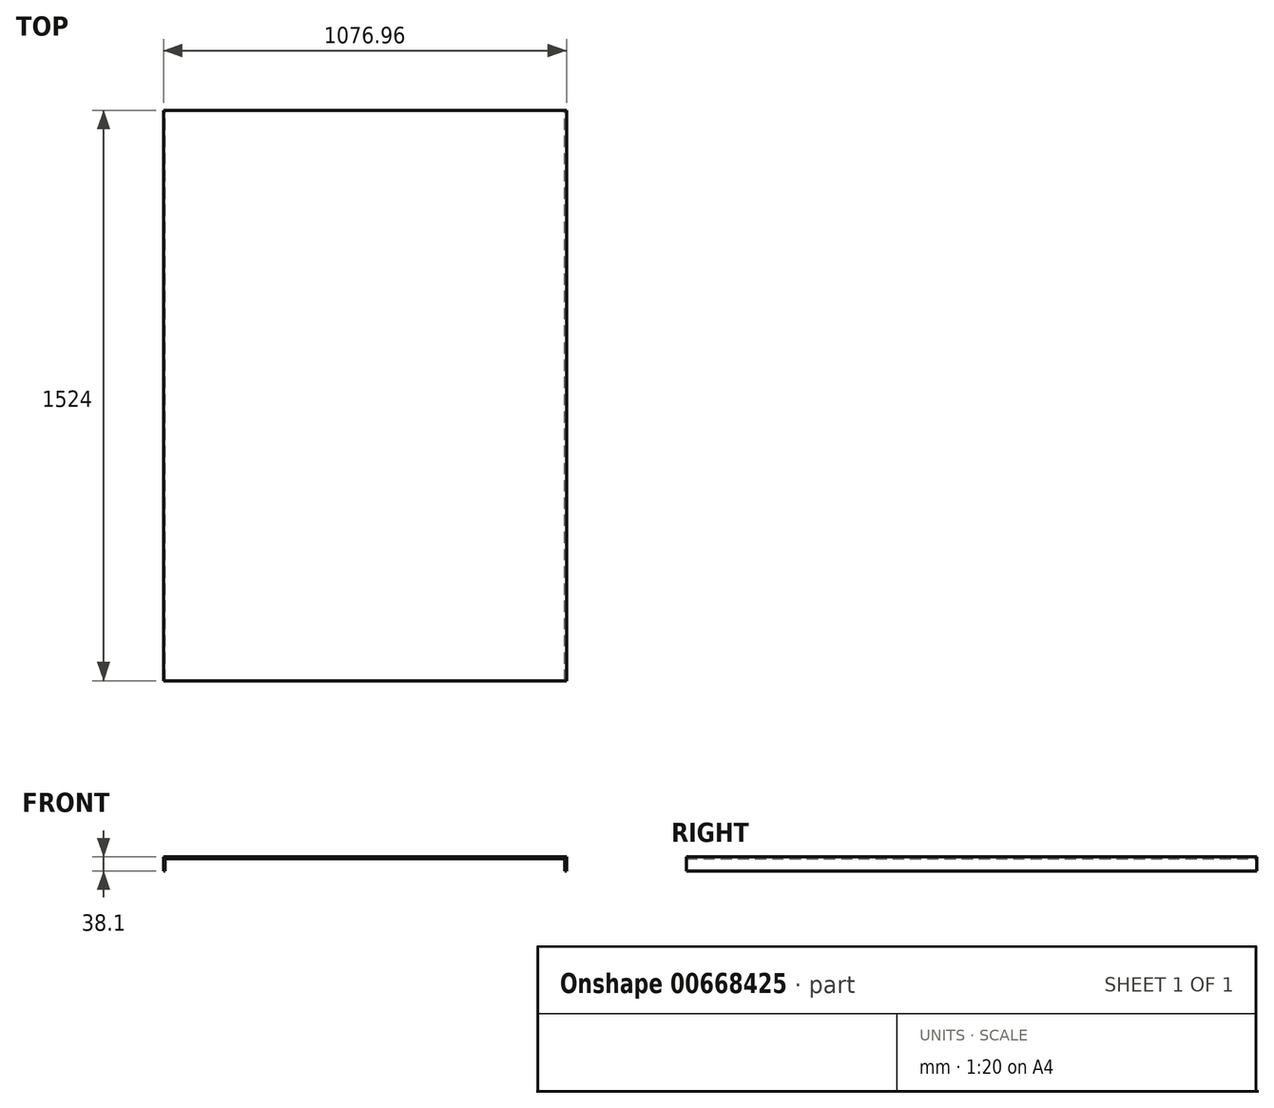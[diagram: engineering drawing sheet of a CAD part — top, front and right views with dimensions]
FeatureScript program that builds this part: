
annotation { "Feature Type Name" : "Feature", "Feature Type Description" : "" }
export const myFeature = defineFeature(function(context is Context, id is Id, definition is map)
    precondition{}
    {
        {
            var Q0;
            Q0=qCreatedBy(makeId("Front.planeOp"),FACE);
            var sketch = newSketch(context, id + "F0", { "sketchPlane" : qUnion([Q0])});
            skLineSegment(sketch, "E0.bottom", {"start": v(-104.04, -41.65) * mm, "end": v(972.92, -41.65) * mm});
            skLineSegment(sketch, "E0.top", {"start": v(-104.04, -36.87) * mm, "end": v(972.92, -36.87) * mm});
            skLineSegment(sketch, "E0.left", {"start": v(-104.04, -41.65) * mm, "end": v(-104.04, -36.87) * mm});
            skLineSegment(sketch, "E0.right", {"start": v(972.92, -41.65) * mm, "end": v(972.92, -36.87) * mm});
            skLineSegment(sketch, "E1.bottom", {"start": v(-104.04, -36.87) * mm, "end": v(-99.27, -36.87) * mm});
            skLineSegment(sketch, "E1.top", {"start": v(-104.04, -74.97) * mm, "end": v(-99.27, -74.97) * mm});
            skLineSegment(sketch, "E1.left", {"start": v(-104.04, -36.87) * mm, "end": v(-104.04, -74.97) * mm});
            skLineSegment(sketch, "E1.right", {"start": v(-99.27, -36.87) * mm, "end": v(-99.27, -74.97) * mm});
            skLineSegment(sketch, "E2.bottom", {"start": v(972.92, -36.87) * mm, "end": v(968.14, -36.87) * mm});
            skLineSegment(sketch, "E2.top", {"start": v(972.92, -74.97) * mm, "end": v(968.14, -74.97) * mm});
            skLineSegment(sketch, "E2.left", {"start": v(972.92, -36.87) * mm, "end": v(972.92, -74.97) * mm});
            skLineSegment(sketch, "E2.right", {"start": v(968.14, -36.87) * mm, "end": v(968.14, -74.97) * mm});
            skSolve(sketch);
        }
        {
            var Q0;
            Q0 = qSketchRegion(id + "F0", true);
            extrude(context, id + "F1", {"entities" : qUnion([Q0]), "depth" : 1524 * mm, "offsetDistance" : 25.4 * mm});
        }
    });
